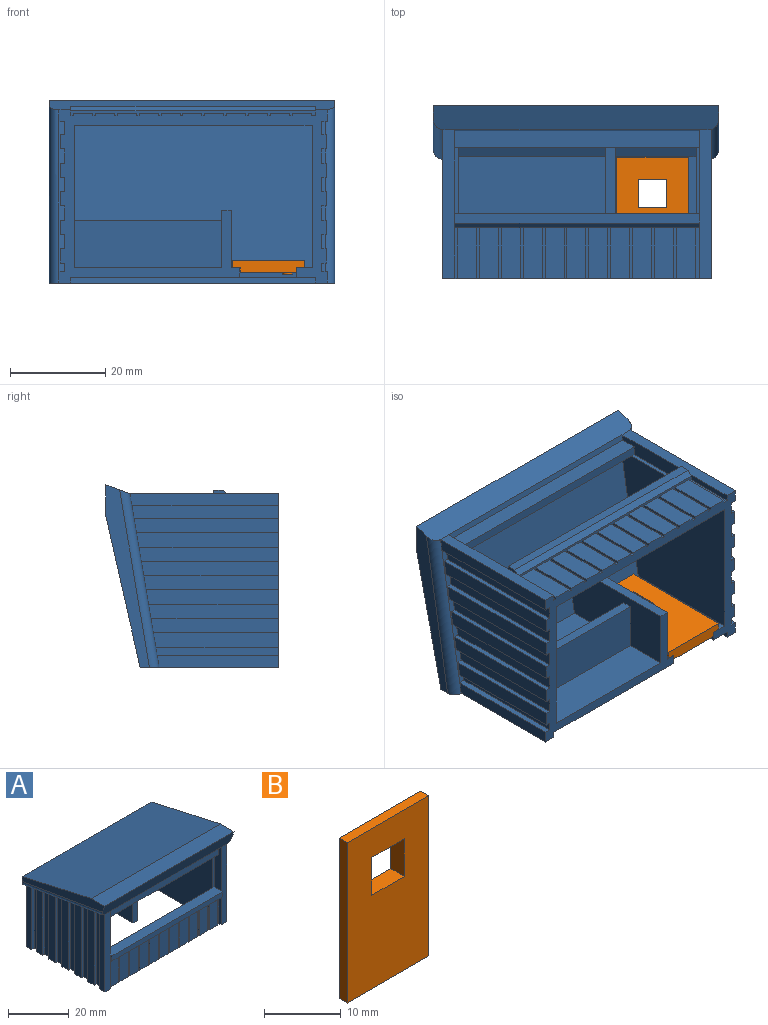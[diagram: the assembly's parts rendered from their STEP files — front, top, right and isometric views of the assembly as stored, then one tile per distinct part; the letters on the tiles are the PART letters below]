
ASSEMBLY  parts=2 mates=1
PART A: 149 faces, bbox 60x38.7x36.4 mm
  f0: plane 31x9mm, normal (0,-1,0), area 279mm2, adj f1,f2,f88,f147
  f1: plane 27.68x12mm, normal (-1,0,0), area 300mm2, adj f0,f25,f26,f88,f143,f146,f147,f148
  f2: plane 30.72x30mm, normal (1,0,0), area 825.7mm2, adj f0,f25,f72,f73,f88,f90,f143,f146
  f3: plane 1.75x0.75mm, normal (0,-0.17,-0.99), area 1.3mm2, adj f62,f63,f64,f145
  f4: plane 3x0.75mm, normal (0,-0.17,-0.99), area 2.3mm2, adj f58,f59,f60,f145
  f5: plane 3x0.75mm, normal (0,-0.17,-0.99), area 2.3mm2, adj f54,f55,f56,f145
  f6: plane 3x0.75mm, normal (0,-0.17,-0.99), area 2.3mm2, adj f50,f51,f52,f145
  f7: plane 3x0.75mm, normal (0,-0.17,-0.99), area 2.3mm2, adj f46,f47,f48,f145
  f8: plane 10.61x0.6mm, normal (0,-1,0), area 6.4mm2, adj f19,f88,f97,f131
  f9: plane 10.61x0.6mm, normal (0,-1,0), area 6.4mm2, adj f88,f96,f99,f131
  f10: plane 10.61x0.6mm, normal (0,-1,0), area 6.4mm2, adj f88,f100,f102,f131
  f11: plane 10.61x0.6mm, normal (0,-1,0), area 6.4mm2, adj f88,f103,f105,f131
  f12: plane 10.61x0.6mm, normal (0,-1,0), area 6.4mm2, adj f88,f106,f108,f131
  f13: plane 10.61x0.6mm, normal (0,-1,0), area 6.4mm2, adj f88,f109,f111,f131
  f14: plane 10.61x0.6mm, normal (0,-1,0), area 6.4mm2, adj f88,f112,f114,f131
  f15: plane 10.61x0.6mm, normal (0,-1,0), area 6.4mm2, adj f88,f115,f117,f131
  f16: plane 10.61x0.6mm, normal (0,-1,0), area 6.4mm2, adj f88,f118,f120,f131
  f17: plane 10.61x0.6mm, normal (0,-1,0), area 6.4mm2, adj f88,f121,f123,f131
  f18: plane 10.61x0.6mm, normal (0,-1,0), area 6.4mm2, adj f88,f124,f126,f131
  f19: plane 10.86x1.25mm, normal (1,0,0), area 13.3mm2, adj f8,f78,f88,f131,f133
  f20: plane 10.86x1.25mm, normal (-1,0,0), area 13.3mm2, adj f21,f82,f88,f131,f133
  f21: plane 10.61x0.9mm, normal (0,-1,0), area 9.6mm2, adj f20,f88,f127,f131
  f22: plane 25.66x17mm, normal (0,-1,0), area 148.2mm2, adj f27,f28,f88,f93,f94,f95,f143
  f23: plane 51.5x25.32mm, normal (0,1,0), area 1016mm2, adj f66,f67,f88,f93,f94,f95,f142
  f24: plane 60x29.11mm, normal (0,1,0), area 363.8mm2, adj f65,f66,f67,f87,f88,f134,f135,f136
  f25: plane 31x14.66mm, normal (0,-1,0), area 454.4mm2, adj f1,f2,f143,f146
  f26: plane 27.68x2mm, normal (0,-1,0), area 55.4mm2, adj f1,f27,f88,f143
  f27: plane 27.68x12mm, normal (1,0,0), area 320mm2, adj f22,f26,f88,f143
  f28: plane 30.72x30mm, normal (-1,0,0), area 845.7mm2, adj f22,f72,f73,f88,f89,f143
  f29: plane 26.33x1mm, normal (0,-1,0), area 26.3mm2, adj f30,f71,f88,f139
  f30: plane 26.84x3mm, normal (-1,0,0), area 79.8mm2, adj f29,f31,f88,f139
  f31: plane 26.84x1mm, normal (0,1,0), area 26.8mm2, adj f30,f32,f88,f139
  f32: plane 27.35x3mm, normal (-1,0,0), area 81.3mm2, adj f31,f33,f88,f139
  f33: plane 27.35x1mm, normal (0,-1,0), area 27.3mm2, adj f32,f34,f88,f139
  f34: plane 27.85x3mm, normal (-1,0,0), area 82.8mm2, adj f33,f35,f88,f139
  f35: plane 27.85x1mm, normal (0,1,0), area 27.9mm2, adj f34,f36,f88,f139
  f36: plane 28.36x3mm, normal (-1,0,0), area 84.3mm2, adj f35,f37,f88,f139
  f37: plane 28.36x1mm, normal (0,-1,0), area 28.4mm2, adj f36,f38,f88,f139
  f38: plane 28.86x3mm, normal (-1,0,0), area 85.8mm2, adj f37,f39,f88,f139
  f39: plane 28.86x1mm, normal (0,1,0), area 28.9mm2, adj f38,f40,f88,f139
  f40: plane 29.37x3mm, normal (-1,0,0), area 87.4mm2, adj f39,f41,f88,f139
  f41: plane 29.37x1mm, normal (0,-1,0), area 29.4mm2, adj f40,f42,f88,f139
  f42: plane 29.88x3mm, normal (-1,0,0), area 88.9mm2, adj f41,f43,f88,f139
  f43: plane 29.88x1mm, normal (0,1,0), area 29.9mm2, adj f42,f44,f88,f139
  f44: plane 30.38x3mm, normal (-1,0,0), area 90.4mm2, adj f43,f74,f88,f139
  f45: plane 30.4x3mm, normal (1,0,0), area 90.4mm2, adj f46,f86,f88,f145
  f46: plane 29.89x1mm, normal (0,1,0), area 29.9mm2, adj f7,f45,f47,f88,f145
  f47: plane 29.88x3mm, normal (1,0,0), area 88.9mm2, adj f7,f46,f48,f88
  f48: plane 29.39x1mm, normal (0,-1,0), area 29.4mm2, adj f7,f47,f49,f88,f145
  f49: plane 29.39x3mm, normal (1,0,0), area 87.4mm2, adj f48,f50,f88,f145
  f50: plane 28.88x1mm, normal (0,1,0), area 28.9mm2, adj f6,f49,f51,f88,f145
  f51: plane 28.86x3mm, normal (1,0,0), area 85.8mm2, adj f6,f50,f52,f88
  f52: plane 28.37x1mm, normal (0,-1,0), area 28.4mm2, adj f6,f51,f53,f88,f145
  f53: plane 28.37x3mm, normal (1,0,0), area 84.4mm2, adj f52,f54,f88,f145
  f54: plane 27.87x1mm, normal (0,1,0), area 27.9mm2, adj f5,f53,f55,f88,f145
  f55: plane 27.85x3mm, normal (1,0,0), area 82.8mm2, adj f5,f54,f56,f88
  f56: plane 27.36x1mm, normal (0,-1,0), area 27.3mm2, adj f5,f55,f57,f88,f145
  f57: plane 27.36x3mm, normal (1,0,0), area 81.3mm2, adj f56,f58,f88,f145
  f58: plane 26.86x1mm, normal (0,1,0), area 26.8mm2, adj f4,f57,f59,f88,f145
  f59: plane 26.84x3mm, normal (1,0,0), area 79.8mm2, adj f4,f58,f60,f88
  f60: plane 26.35x1mm, normal (0,-1,0), area 26.3mm2, adj f4,f59,f61,f88,f145
  f61: plane 26.35x3mm, normal (1,0,0), area 78.3mm2, adj f60,f62,f88,f145
  f62: plane 25.84x1mm, normal (0,1,0), area 25.8mm2, adj f3,f61,f63,f88,f145
  f63: plane 25.83x1.75mm, normal (1,0,0), area 44.9mm2, adj f3,f62,f64,f88
  f64: plane 25.6x1.26mm, normal (0,-1,0), area 31.9mm2, adj f3,f63,f65,f88,f145
  f65: plane 25.6x2.5mm, normal (1,0,0), area 63.5mm2, adj f24,f64,f88,f145
  f66: plane 25.32x1.25mm, normal (-1,0,0), area 31.5mm2, adj f23,f24,f88,f142
  f67: plane 25.32x1.25mm, normal (1,0,0), area 31.5mm2, adj f23,f24,f88,f142
  f68: plane 25.53x1.25mm, normal (0,-1,0), area 31.9mm2, adj f69,f87,f88,f139
  f69: plane 25.83x1.75mm, normal (-1,0,0), area 44.9mm2, adj f68,f70,f88,f139
  f70: plane 25.83x1mm, normal (0,1,0), area 25.8mm2, adj f69,f71,f88,f139
  f71: plane 26.33x3mm, normal (-1,0,0), area 78.2mm2, adj f29,f70,f88,f139
  f72: plane 50x3.11mm, normal (0,1,0), area 155.3mm2, adj f2,f28,f91,f143
  f73: plane 50x13.61mm, normal (0,1,0), area 680.7mm2, adj f2,f28,f88,f92
  f74: plane 30.38x1mm, normal (0,-1,0), area 30.4mm2, adj f44,f75,f88,f139
  f75: plane 30.85x2.75mm, normal (-1,0,0), area 84.2mm2, adj f74,f76,f88,f139
  f76: plane 30.85x1.25mm, normal (0,1,0), area 38.6mm2, adj f75,f77,f88,f139
  f77: plane 31.27x2.5mm, normal (-1,0,0), area 77.6mm2, adj f76,f78,f88,f144
  f78: plane 31.27x2.5mm, normal (0,-1,0), area 78.2mm2, adj f19,f77,f79,f88,f129,f138
  f79: plane 17.65x3.25mm, normal (1,0,0), area 49.9mm2, adj f78,f80,f90,f91,f92,f141
  f80: plane 51.5x3.44mm, normal (0,-1,0), area 177.3mm2, adj f79,f81,f91,f141
  f81: plane 17.65x3.25mm, normal (-1,0,0), area 49.9mm2, adj f80,f82,f89,f91,f92,f141
  f82: plane 31.34x2.51mm, normal (0,-1,0), area 78.2mm2, adj f20,f81,f83,f88,f130,f138,f145
  f83: plane 31.33x2.5mm, normal (1,0,0), area 77.8mm2, adj f82,f84,f88,f145
  f84: plane 30.92x1.26mm, normal (0,1,0), area 38.6mm2, adj f83,f85,f88,f140,f145
  f85: plane 30.85x2.75mm, normal (1,0,0), area 84.2mm2, adj f84,f86,f88,f140
  f86: plane 30.4x1mm, normal (0,-1,0), area 30.4mm2, adj f45,f85,f88,f140,f145
  f87: plane 25.53x2.5mm, normal (-1,0,0), area 63.3mm2, adj f24,f68,f88,f144
  f88: plane 56.5x36.5mm, normal (0,0,-1), area 406.7mm2, adj f0,f1,f2,f8,f9,f10,f11,f12
  f89: plane 14x0.75mm, normal (0,-1,0), area 10.5mm2, adj f28,f81,f91,f92
  f90: plane 14x0.75mm, normal (0,-1,0), area 10.5mm2, adj f2,f79,f91,f92
  f91: plane 51.5x2mm, normal (0,0,-1), area 103mm2, adj f72,f79,f80,f81,f89,f90
  f92: plane 51.5x4mm, normal (0,0,1), area 206mm2, adj f73,f79,f81,f89,f90,f129,f130,f132
  f93: plane 24x2mm, normal (1,0,0), area 48mm2, adj f22,f23,f88,f94
  f94: plane 12x2mm, normal (0,0,-1), area 24mm2, adj f22,f23,f93,f95
  f95: plane 24x2mm, normal (-1,0,0), area 48mm2, adj f22,f23,f88,f94
  f96: plane 10.61x0.5mm, normal (1,0,0), area 5.3mm2, adj f9,f88,f98,f131
  f97: plane 10.61x0.5mm, normal (-1,0,0), area 5.3mm2, adj f8,f88,f98,f131
  f98: plane 10.61x4mm, normal (0,-1,0), area 42.5mm2, adj f88,f96,f97,f131
  f99: plane 10.61x0.5mm, normal (-1,0,0), area 5.3mm2, adj f9,f88,f101,f131
  f100: plane 10.61x0.5mm, normal (1,0,0), area 5.3mm2, adj f10,f88,f101,f131
  f101: plane 10.61x4mm, normal (0,-1,0), area 42.5mm2, adj f88,f99,f100,f131
  f102: plane 10.61x0.5mm, normal (-1,0,0), area 5.3mm2, adj f10,f88,f104,f131
  f103: plane 10.61x0.5mm, normal (1,0,0), area 5.3mm2, adj f11,f88,f104,f131
  f104: plane 10.61x4mm, normal (0,-1,0), area 42.5mm2, adj f88,f102,f103,f131
  f105: plane 10.61x0.5mm, normal (-1,0,0), area 5.3mm2, adj f11,f88,f107,f131
  f106: plane 10.61x0.5mm, normal (1,0,0), area 5.3mm2, adj f12,f88,f107,f131
  f107: plane 10.61x4mm, normal (0,-1,0), area 42.5mm2, adj f88,f105,f106,f131
  f108: plane 10.61x0.5mm, normal (-1,0,0), area 5.3mm2, adj f12,f88,f110,f131
  f109: plane 10.61x0.5mm, normal (1,0,0), area 5.3mm2, adj f13,f88,f110,f131
  f110: plane 10.61x4mm, normal (0,-1,0), area 42.5mm2, adj f88,f108,f109,f131
  f111: plane 10.61x0.5mm, normal (-1,0,0), area 5.3mm2, adj f13,f88,f113,f131
  f112: plane 10.61x0.5mm, normal (1,0,0), area 5.3mm2, adj f14,f88,f113,f131
  f113: plane 10.61x4mm, normal (0,-1,0), area 42.5mm2, adj f88,f111,f112,f131
  f114: plane 10.61x0.5mm, normal (-1,0,0), area 5.3mm2, adj f14,f88,f116,f131
  f115: plane 10.61x0.5mm, normal (1,0,0), area 5.3mm2, adj f15,f88,f116,f131
  f116: plane 10.61x4mm, normal (0,-1,0), area 42.5mm2, adj f88,f114,f115,f131
  f117: plane 10.61x0.5mm, normal (-1,0,0), area 5.3mm2, adj f15,f88,f119,f131
  f118: plane 10.61x0.5mm, normal (1,0,0), area 5.3mm2, adj f16,f88,f119,f131
  f119: plane 10.61x4mm, normal (0,-1,0), area 42.5mm2, adj f88,f117,f118,f131
  f120: plane 10.61x0.5mm, normal (-1,0,0), area 5.3mm2, adj f16,f88,f122,f131
  f121: plane 10.61x0.5mm, normal (1,0,0), area 5.3mm2, adj f17,f88,f122,f131
  f122: plane 10.61x4mm, normal (0,-1,0), area 42.5mm2, adj f88,f120,f121,f131
  f123: plane 10.61x0.5mm, normal (-1,0,0), area 5.3mm2, adj f17,f88,f125,f131
  f124: plane 10.61x0.5mm, normal (1,0,0), area 5.3mm2, adj f18,f88,f125,f131
  f125: plane 10.61x4mm, normal (0,-1,0), area 42.5mm2, adj f88,f123,f124,f131
  f126: plane 10.61x0.5mm, normal (-1,0,0), area 5.3mm2, adj f18,f88,f128,f131
  f127: plane 10.61x0.5mm, normal (1,0,0), area 5.3mm2, adj f21,f88,f128,f131
  f128: plane 10.61x4mm, normal (0,-1,0), area 42.5mm2, adj f88,f126,f127,f131
  f129: plane 2.75x0.75mm, normal (-1,0,0), area 1.8mm2, adj f78,f92,f132,f133
  f130: plane 2.75x0.75mm, normal (1,0,0), area 1.8mm2, adj f82,f92,f132,f133
  f131: plane 51.5x1mm, normal (0,0,-1), area 29.5mm2, adj f8,f9,f10,f11,f12,f13,f14,f15
  f132: plane 51.5x2mm, normal (0,-1,0), area 103mm2, adj f92,f129,f130,f133
  f133: plane 51.5x1mm, normal (0,-0.71,-0.71), area 72.8mm2, adj f19,f20,f129,f130,f131,f132
  f134: plane 38.38x9.24mm, normal (-1,0,0), area 111.8mm2, adj f24,f136,f137,f138,f144
  f135: plane 38.38x9.24mm, normal (1,0,0), area 111.8mm2, adj f24,f136,f137,f138,f145
  f136: plane 60x32.17mm, normal (0,0.22,0.98), area 1978.7mm2, adj f24,f134,f135,f137
  f137: plane 60x6.21mm, normal (0,-0.01,1), area 372.9mm2, adj f134,f135,f136,f138
  f138: plane 60x5.06mm, normal (0,-0.94,-0.35), area 321.6mm2, adj f78,f82,f134,f135,f137,f141,f144,f145
  f139: plane 31.5x5.32mm, normal (0,-0.17,-0.99), area 24.7mm2, adj f29,f30,f31,f32,f33,f34,f35,f36
  f140: plane 2.75x0.75mm, normal (0,-0.17,-0.99), area 2.1mm2, adj f84,f85,f86,f145
  f141: plane 51.5x1.25mm, normal (0,-0.17,-0.99), area 65.3mm2, adj f79,f80,f81,f138
  f142: plane 51.5x1.25mm, normal (0,-0.17,-0.99), area 65.3mm2, adj f23,f24,f66,f67
  f143: plane 50x30mm, normal (0,-0.17,-0.99), area 1496.9mm2, adj f1,f2,f22,f25,f26,f27,f28,f72
  f144: cylinder r=2mm len=37.97mm, axis (0,-0.99,0.17), area 117.2mm2, adj f24,f77,f87,f134,f138,f139
  f145: cylinder r=2mm len=37.96mm, axis (0,0.99,-0.17), area 110.8mm2, adj f3,f4,f5,f6,f7,f24,f45,f46
  f146: plane 31x10mm, normal (0,0,1), area 310mm2, adj f1,f2,f25,f148
  f147: plane 31x10mm, normal (0,0,-1), area 310mm2, adj f0,f1,f2,f148
  f148: plane 31x2mm, normal (0,-1,0), area 62mm2, adj f1,f2,f146,f147
PART B: 16 faces, bbox 15x3x25.5 mm
  f0: plane 25.5x15mm, normal (0,-1,0), area 346.5mm2, adj f3,f4,f5,f6,f10,f11,f12,f13
  f1: plane 23.9x11.8mm, normal (0,1,0), area 242.9mm2, adj f4,f7,f8,f9,f10,f11,f12,f13
  f2: plane 25.5x15mm, normal (0,1,0), area 100.5mm2, adj f3,f4,f5,f6,f7,f8,f9
  f3: plane 25.5x1.5mm, normal (1,0,0), area 38.3mm2, adj f0,f2,f4,f6
  f4: plane 15x2.5mm, normal (0,0,-1), area 34.3mm2, adj f0,f1,f2,f3,f5,f7,f9
  f5: plane 25.5x1.5mm, normal (-1,0,0), area 38.3mm2, adj f0,f2,f4,f6
  f6: plane 15x1.5mm, normal (0,0,1), area 22.5mm2, adj f0,f2,f3,f5
  f7: plane 23.9x1mm, normal (-1,0,0), area 23.9mm2, adj f1,f2,f4,f8
  f8: plane 11.8x1mm, normal (0,0,1), area 11.8mm2, adj f1,f2,f7,f9
  f9: plane 23.9x1mm, normal (1,0,0), area 23.9mm2, adj f1,f2,f4,f8
  f10: plane 6x2.5mm, normal (0,0,1), area 15mm2, adj f0,f1,f11,f13
  f11: plane 6x2.5mm, normal (1,0,0), area 15mm2, adj f0,f1,f10,f12
  f12: plane 6x2.5mm, normal (0,0,-1), area 15mm2, adj f0,f1,f11,f13
  f13: plane 6x2.5mm, normal (-1,0,0), area 15mm2, adj f0,f1,f10,f12
  f14: cylinder r=1mm len=2mm, axis (0,-1,0), area 3.1mm2, adj f1,f15
  f15: plane 2x2mm, normal (0,1,0), area 3.1mm2, adj f14
PLACE A rot(axis=(-1,0,0),90deg) t=(2.09,26.44,18.4)mm
PLACE B rot(axis=(-1,0,0),90deg) t=(2.19,26.44,20.4)mm
MATE fastened B.f2 <-> A.f22  axis (0,0,-1) through (23.84,26.44,3.4)mm
